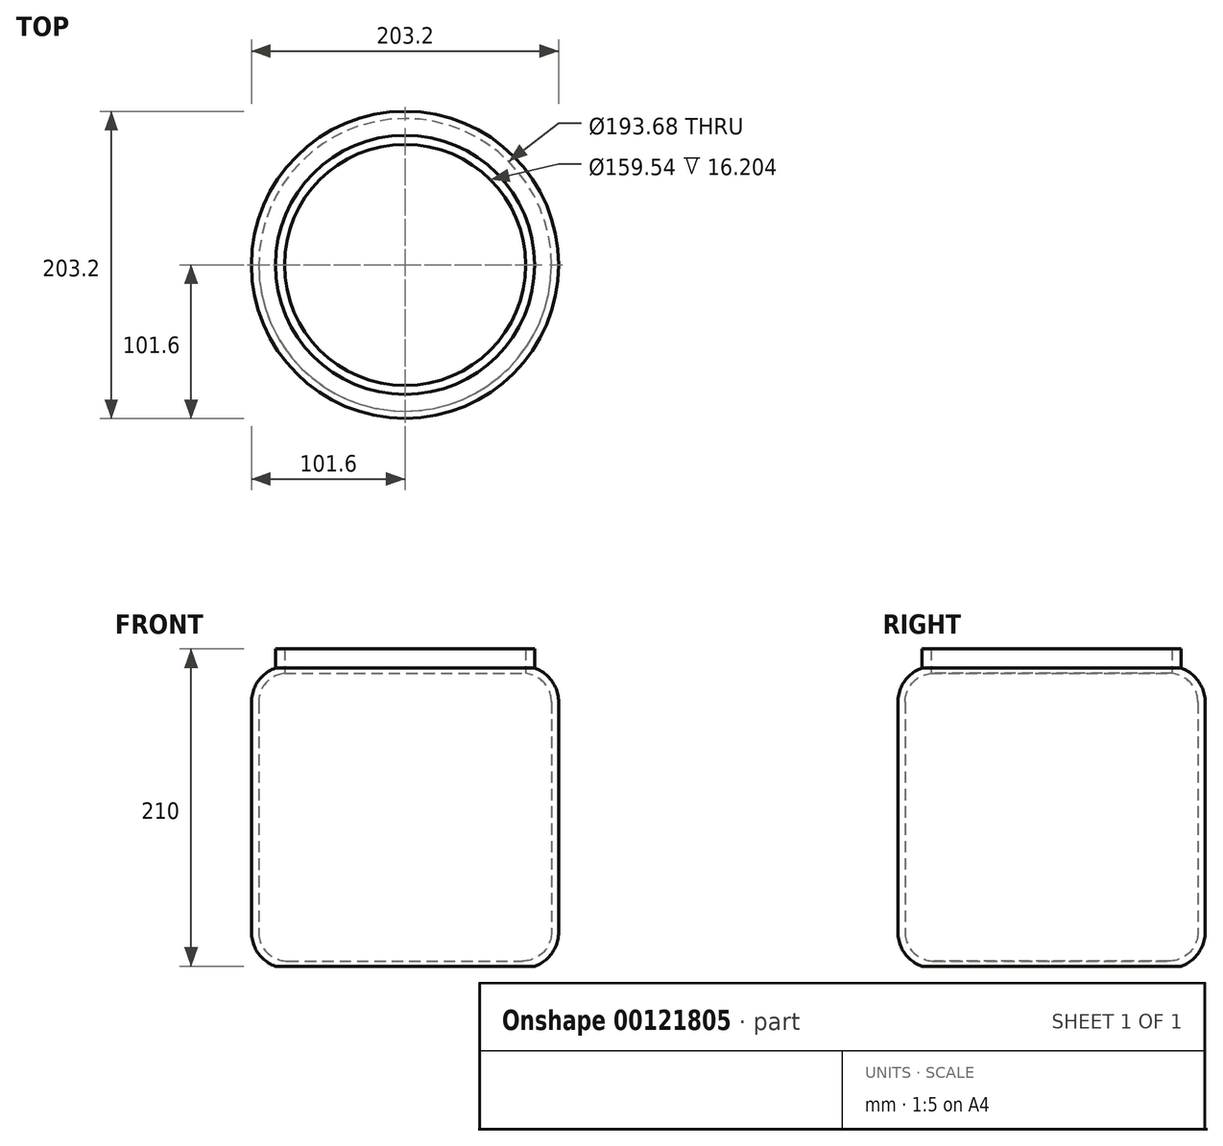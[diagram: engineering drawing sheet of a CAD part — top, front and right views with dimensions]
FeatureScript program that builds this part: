
annotation { "Feature Type Name" : "Feature", "Feature Type Description" : "" }
export const myFeature = defineFeature(function(context is Context, id is Id, definition is map)
    precondition{}
    {
        {
            var Q0;
            Q0=qCreatedBy(makeId("Top.planeOp"),FACE);
            var sketch = newSketch(context, id + "F0", { "sketchPlane" : qUnion([Q0])});
            skCircle(sketch, "E0", {"center": v(0, 0) * mm, "radius": 101.6 * mm});
            skCircle(sketch, "E1", {"center": v(0, 0) * mm, "radius": 96.84 * mm});
            skSolve(sketch);
        }
        {
            var Q0;
            Q0=makeQuery(id+"F0.imprint","IMPRINT",FACE,{"disambiguationData":[TD([[makeQuery(id+"F0.imprint","IMPRINT",EDGE,{"derivedFrom":sQuery(id+"F0.wireOp",EDGE,"E0")}),1.0]])]});
            extrude(context, id + "F1", {"entities" : qUnion([Q0]), "depth" : 152.4 * mm});
        }
        {
            var Q0;
            Q0=qCreatedBy(makeId("Right.planeOp"),FACE);
            var sketch = newSketch(context, id + "F2", { "sketchPlane" : qUnion([Q0])});
            skLineSegment(sketch, "E2", {"start": v(0, 0) * mm, "end": v(0, 152.4) * mm});
            skLineSegment(sketch, "E3", {"start": v(0, 152.4) * mm, "end": v(-96.84, 152.4) * mm});
            skLineSegment(sketch, "E4", {"start": v(-96.84, 152.4) * mm, "end": v(-77.79, 152.4) * mm});
            skLineSegment(sketch, "E5", {"start": v(-77.79, 152.4) * mm, "end": v(-77.79, 171.45) * mm});
            skArc(sketch, "E6", {"start": v(-77.79, 171.45) * mm, "mid": v(-91.26, 165.87) * mm, "end": v(-96.84, 152.4) * mm});
            skLineSegment(sketch, "E7", {"start": v(-96.84, 152.4) * mm, "end": v(-101.6, 152.4) * mm});
            skLineSegment(sketch, "E8", {"start": v(-77.79, 171.45) * mm, "end": v(-77.79, 176.21) * mm});
            skArc(sketch, "E9", {"start": v(-77.79, 176.21) * mm, "mid": v(-94.63, 169.24) * mm, "end": v(-101.6, 152.4) * mm});
            skLineSegment(sketch, "E10", {"start": v(-77.79, 152.4) * mm, "end": v(-85.73, 152.4) * mm});
            skLineSegment(sketch, "E11", {"start": v(-85.73, 152.4) * mm, "end": v(-85.73, 169.72) * mm});
            skLineSegment(sketch, "E12", {"start": v(-85.73, 174.85) * mm, "end": v(-77.79, 174.85) * mm});
            skLineSegment(sketch, "E13", {"start": v(-81.76, 174.85) * mm, "end": v(-77.79, 174.85) * mm});
            skLineSegment(sketch, "E14", {"start": v(-79.77, 174.85) * mm, "end": v(-79.77, 171.35) * mm});
            skSolve(sketch);
        }
        {
            var Q0;
            {var subQ4=sQuery(id+"F2.wireOp",EDGE,"E7");Q0=makeQuery(id+"F2.imprint","IMPRINT",FACE,{"disambiguationData":[TD([[makeQuery(id+"F2.imprint","IMPRINT",EDGE,{"derivedFrom":subQ4}),-1.0]])]});}
            var Q1;
            Q1=sQuery(id+"F2.wireOp",EDGE,"E2");
            revolve(context, id + "F3", {"operationType" : NewBodyOperationType.ADD, "entities" : qUnion([Q0]), "axis" : qUnion([Q1]), "revolveType" : RevolveType.FULL});
        }
        {
            var Q0;
            Q0=makeQuery(id+"F3.opRevolve","SWEPT_FACE",FACE,{"disambiguationData":[OSD([sQuery(id+"F2.wireOp",EDGE,"E12")])]});
            extrude(context, id + "F4", {"entities" : qUnion([Q0]), "operationType" : NewBodyOperationType.ADD, "depth" : 12.7 * mm});
        }
        {
            var Q0;
            Q0=qCreatedBy(makeId("Right.planeOp"),FACE);
            var sketch = newSketch(context, id + "F5", { "sketchPlane" : qUnion([Q0])});
            skLineSegment(sketch, "E15", {"start": v(0, 0) * mm, "end": v(-96.84, 0) * mm});
            skLineSegment(sketch, "E16", {"start": v(-96.84, 0) * mm, "end": v(-77.79, 0) * mm});
            skLineSegment(sketch, "E17", {"start": v(-77.79, 0) * mm, "end": v(-77.79, -19.05) * mm});
            skArc(sketch, "E18", {"start": v(-96.84, 0) * mm, "mid": v(-91.26, -13.47) * mm, "end": v(-77.79, -19.05) * mm});
            skLineSegment(sketch, "E19", {"start": v(-96.84, 0) * mm, "end": v(-101.6, 0) * mm});
            skArc(sketch, "E20", {"start": v(-101.6, 0) * mm, "mid": v(-97.23, -13.75) * mm, "end": v(-85.73, -22.45) * mm});
            skLineSegment(sketch, "E21", {"start": v(-77.79, 0) * mm, "end": v(-85.73, 0) * mm});
            skLineSegment(sketch, "E22", {"start": v(-85.73, 0) * mm, "end": v(-85.73, -17.32) * mm});
            skLineSegment(sketch, "E23", {"start": v(-85.73, -22.45) * mm, "end": v(-77.79, -22.45) * mm});
            skLineSegment(sketch, "E24", {"start": v(-77.79, -22.45) * mm, "end": v(0, -22.45) * mm});
            skLineSegment(sketch, "E25", {"start": v(0, -22.45) * mm, "end": v(0, 0) * mm});
            skLineSegment(sketch, "E26", {"start": v(-77.79, -19.05) * mm, "end": v(0, -19.05) * mm});
            skSolve(sketch);
        }
        {
            var Q0;
            {var subQ1=sQuery(id+"F5.wireOp",EDGE,"E19");Q0=makeQuery(id+"F5.imprint","IMPRINT",FACE,{"disambiguationData":[TD([[makeQuery(id+"F5.imprint","IMPRINT",EDGE,{"derivedFrom":subQ1}),1.0]])]});}
            var Q1;
            Q1=sQuery(id+"F5.wireOp",EDGE,"E25");
            revolve(context, id + "F6", {"operationType" : NewBodyOperationType.ADD, "entities" : qUnion([Q0]), "axis" : qUnion([Q1]), "revolveType" : RevolveType.FULL});
        }
    });
